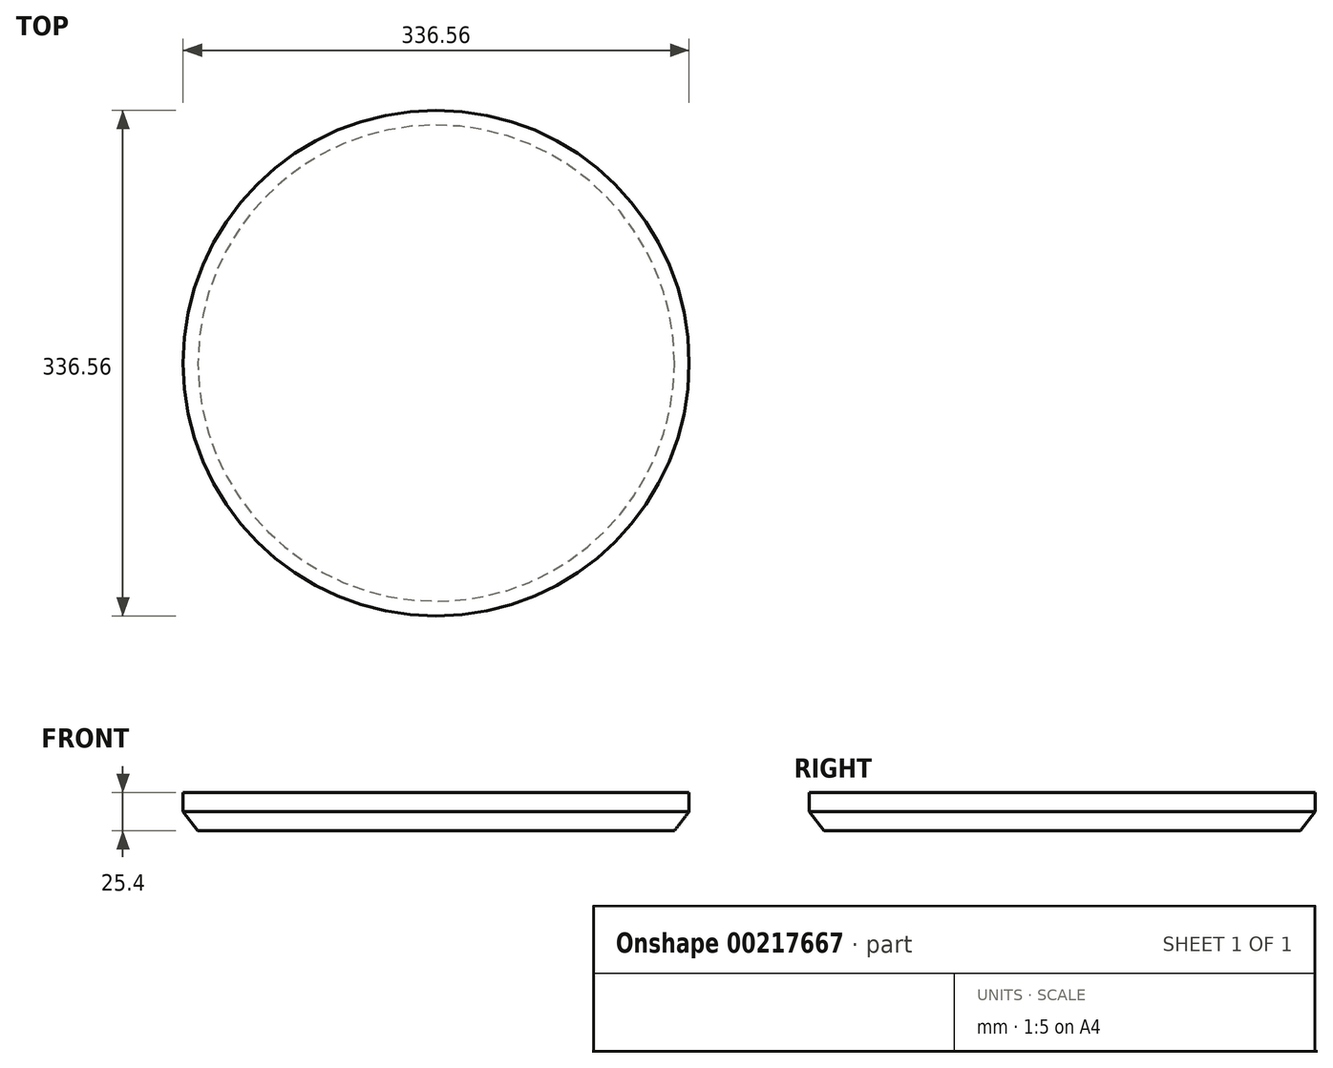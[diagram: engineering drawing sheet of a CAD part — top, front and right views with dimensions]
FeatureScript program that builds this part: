
annotation { "Feature Type Name" : "Feature", "Feature Type Description" : "" }
export const myFeature = defineFeature(function(context is Context, id is Id, definition is map)
    precondition{}
    {
        {
            var Q0;
            Q0=qCreatedBy(makeId("Front.planeOp"),FACE);
            var sketch = newSketch(context, id + "F0", { "sketchPlane" : qUnion([Q0])});
            skLineSegment(sketch, "E0", {"start": v(0, 0) * mm, "end": v(158.46, 0) * mm});
            skLineSegment(sketch, "E1", {"start": v(168.28, 12.7) * mm, "end": v(168.28, 25.4) * mm});
            skLineSegment(sketch, "E2", {"start": v(168.28, 25.4) * mm, "end": v(0, 25.4) * mm});
            skLineSegment(sketch, "E3", {"start": v(0, 25.4) * mm, "end": v(0, 0) * mm});
            skLineSegment(sketch, "E4", {"start": v(168.28, 12.7) * mm, "end": v(158.46, 0) * mm});
            skPoint(sketch, "E5.orphan", {"position": v(168.28, 0) * mm});
            skSolve(sketch);
        }
        {
            var Q0;
            Q0 = qSketchRegion(id + "F0", true);
            var Q1;
            Q1=sQuery(id+"F0.wireOp",EDGE,"E3");
            revolve(context, id + "F1", {"entities" : qUnion([Q0]), "axis" : qUnion([Q1]), "revolveType" : RevolveType.FULL});
        }
    });
